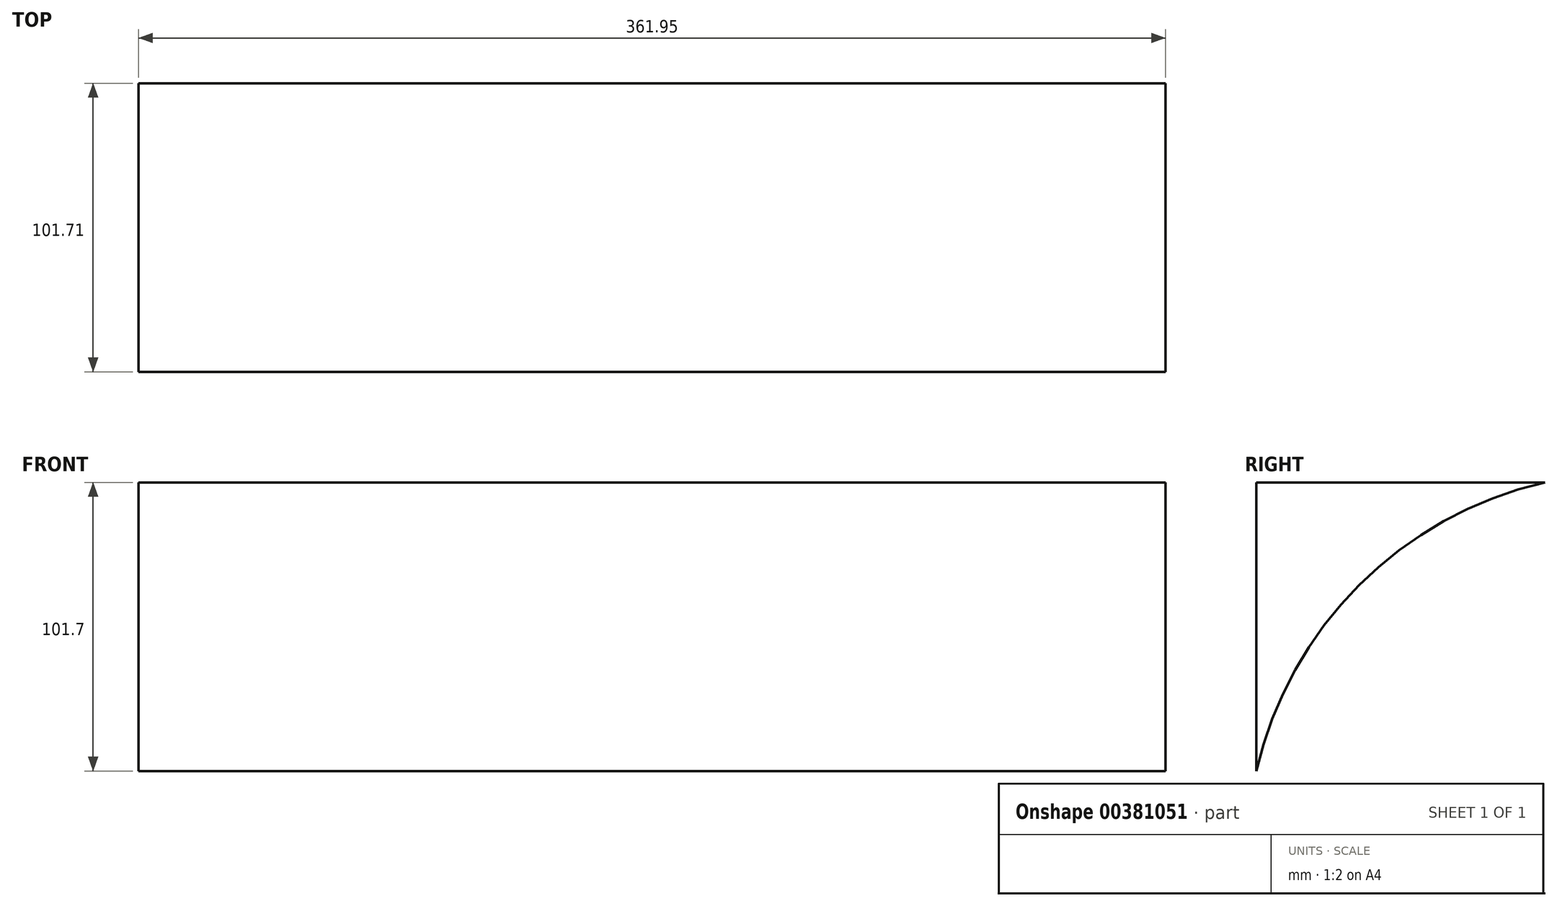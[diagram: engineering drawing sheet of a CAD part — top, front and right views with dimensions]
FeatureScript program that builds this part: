
annotation { "Feature Type Name" : "Feature", "Feature Type Description" : "" }
export const myFeature = defineFeature(function(context is Context, id is Id, definition is map)
    precondition{}
    {
        {
            var Q0;
            Q0=qCreatedBy(makeId("Right.planeOp"),FACE);
            var sketch = newSketch(context, id + "F0", { "sketchPlane" : qUnion([Q0])});
            skLineSegment(sketch, "E0", {"start": v(-76.23, 0) * mm, "end": v(-76.23, 101.7) * mm});
            skLineSegment(sketch, "E1", {"start": v(-76.23, 101.7) * mm, "end": v(25.48, 101.7) * mm});
            skArc(sketch, "E2", {"start": v(25.48, 101.7) * mm, "mid": v(-40.01, 65.5) * mm, "end": v(-76.23, 0) * mm});
            skSolve(sketch);
        }
        {
            var Q0;
            Q0=makeQuery(id+"F0.imprint","IMPRINT",FACE,{"disambiguationData":[TD([[makeQuery(id+"F0.imprint","IMPRINT",EDGE,{"derivedFrom":sQuery(id+"F0.wireOp",EDGE,"E0")}),-1.0]])]});
            extrude(context, id + "F1", {"entities" : qUnion([Q0]), "depth" : 361.95 * mm});
        }
    });
